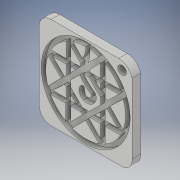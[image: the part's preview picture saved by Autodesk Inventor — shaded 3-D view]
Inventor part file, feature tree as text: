
AUTODESK INVENTOR PART (.ipt)
format: ipt  version: 2017 (Build 210142000, 142)  size: 350,208 bytes
history: native  units: in
note: dims shown in document units (in); Inventor stores cm internally (conversion verified against a paired STEP export)
features: extrude x4, sketch x3, other x1
ambient origin geometry x8: Origin, YZ Plane, XZ Plane, XY Plane, X Axis, Y Axis, Z Axis, Center Point
bodies: Solid1 (feature_tree)
feature tree (8):
  sketch  "Sketch1"  dims[d0=3.0in d1=3.0in]
  extrude  "Extrusion1"  Depth=3.0in
  extrude  "Extrusion2"  Depth=0.125in TaperAngle=0.0deg
  sketch  "Sketch5"  dims[d39=0.1271in d40=0.136in d41=0.136in d42=0.125in d43=0.1262in d44=0.1336in d45=0.1349in d46=0.1262in d47=0.1262in d48=0.14in d49=0.1271in d50=0.136in d51=0.137in d52=0.1443in d53=0.125in d54=0.0in d55=2.025in d56=2.025in d57=0.25in d58=0.0in d59=0.0in d60=0.0in d61=0.0in]
  extrude  "Extrusion3"  Depth=0.25in
  extrude  "Extrusion4"  Depth=0.25in
  other  "Image1"
  sketch  "Sketch4"  dims[d20=0.25in d21=0.0in]
